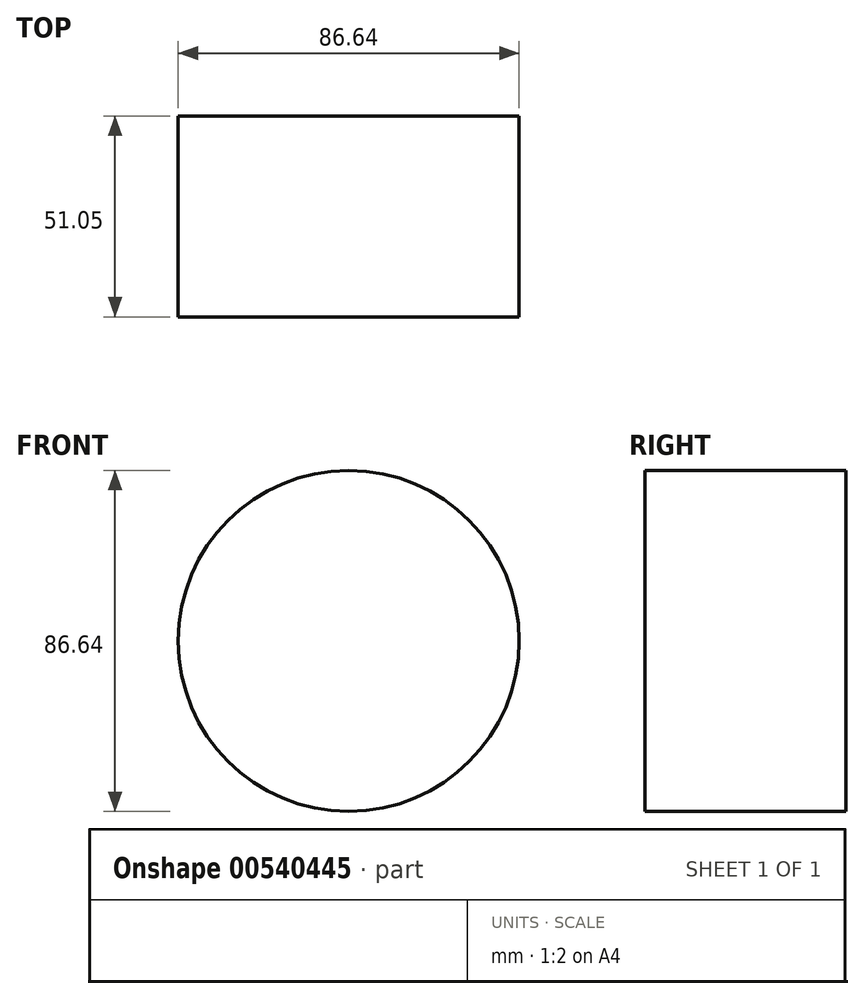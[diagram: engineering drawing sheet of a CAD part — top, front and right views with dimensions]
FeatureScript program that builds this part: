
annotation { "Feature Type Name" : "Feature", "Feature Type Description" : "" }
export const myFeature = defineFeature(function(context is Context, id is Id, definition is map)
    precondition{}
    {
        {
            var Q0;
            Q0=qCreatedBy(makeId("Front.planeOp"),FACE);
            var sketch = newSketch(context, id + "F0", { "sketchPlane" : qUnion([Q0])});
            skCircle(sketch, "E0", {"center": v(0, 0) * mm, "radius": 43.32 * mm});
            skSolve(sketch);
        }
        {
            var Q0;
            Q0=makeQuery(id+"F0.imprint","IMPRINT",FACE,{"disambiguationData":[TD([[makeQuery(id+"F0.imprint","IMPRINT",EDGE,{"derivedFrom":sQuery(id+"F0.wireOp",EDGE,"E0")}),1.0]])]});
            extrude(context, id + "F1", {"entities" : qUnion([Q0]), "oppositeDirection" : true, "depth" : 51.05 * mm, "offsetDistance" : 25.4 * mm});
        }
    });
